# Revit family: C_FP40_2_25_2DO_CAD_MULT_Prod
name_source: partatom
category: Detail Items
revit_build: Autodesk Revit 2015 (Build: 20140606_1530(x64)
units: mm (PartAtom-declared; Revit-internal decimal feet)

## types (2) — shared parameters
Density = 14.00 kg
Description = Straps
EPD = https://www.strongtie.eu
ETA / DoP = https://www.strongtie.eu
Manufacturer = Simpson Strong-Tie
Model = FP40/2/25
Model Disclaimer = Contact Simpson Strong-Tie Company  for more information
Model ID = 0299038447722393878309673721917997378135
Name = FP40/2/25
ObjectType = FP40/2/25
Product Material = Galvanised
Product Type = Straps
Reference = FP40/2/25
Technical datasheet = https://www.strongtie.eu
URL = www.strongtie.eu
UniClass Number = Pr_20_29_31_13
UniClass Title = Carbon steel punched metal plate fasteners

## per-type parameters (varying)
| type | _visiblefront | _visibleleft |
| SST_FP40/2/25_Front | Yes | No |
| SST_FP40/2/25_Left | No | Yes |

## geometry (parser evidence)
native form markers: Sweep x5
no freeform markers — native parametric forms only
